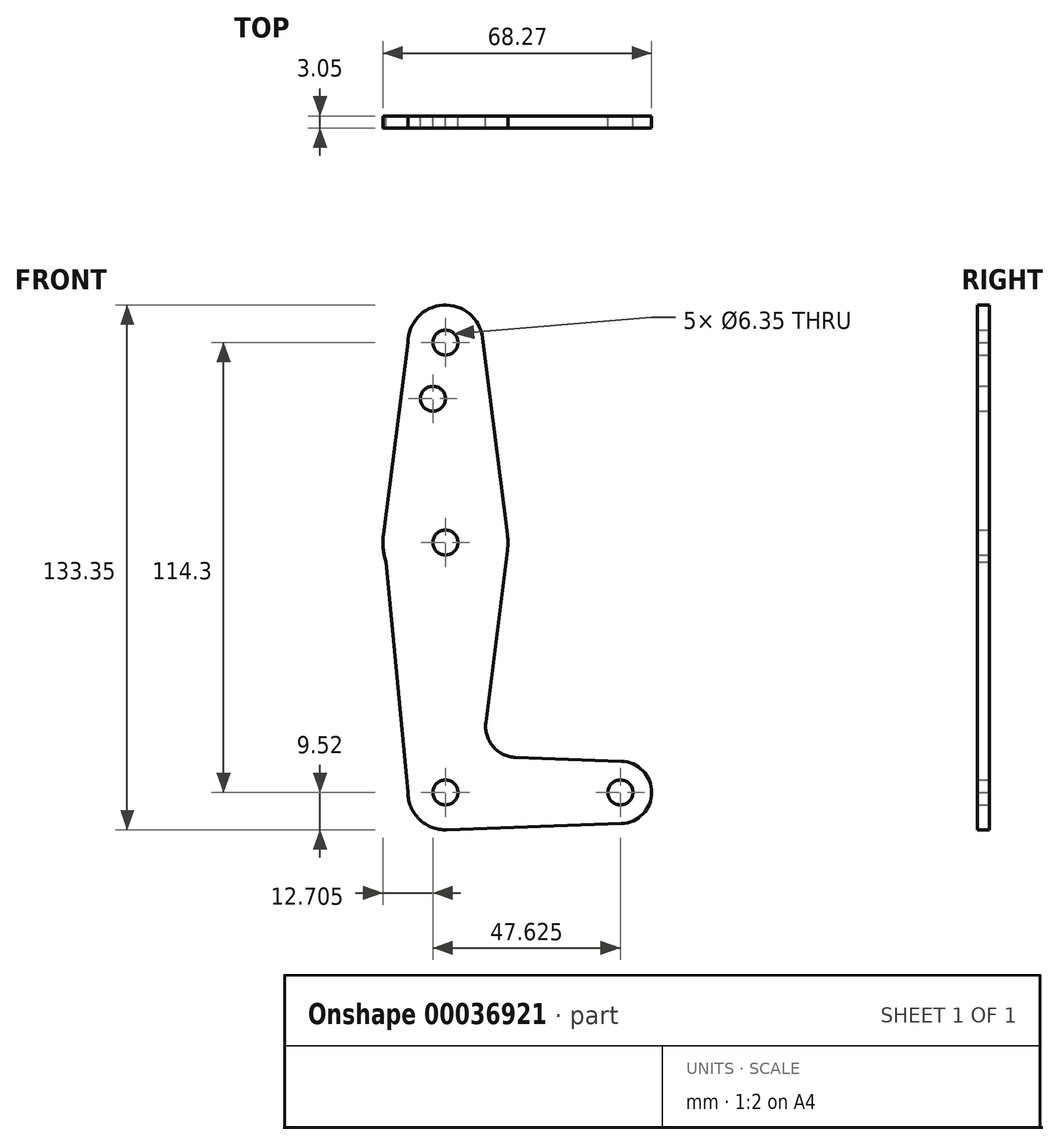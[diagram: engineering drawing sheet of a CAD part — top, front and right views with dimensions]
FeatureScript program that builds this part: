
annotation { "Feature Type Name" : "Feature", "Feature Type Description" : "" }
export const myFeature = defineFeature(function(context is Context, id is Id, definition is map)
    precondition{}
    {
        {
            var Q0;
            Q0=qCreatedBy(makeId("Front.planeOp"),FACE);
            var sketch = newSketch(context, id + "F0", { "sketchPlane" : qUnion([Q0])});
            skCircle(sketch, "E0", {"center": v(0, 63.5) * mm, "radius": 15.88 * mm});
            skCircle(sketch, "E1", {"center": v(0, 114.3) * mm, "radius": 9.53 * mm});
            skCircle(sketch, "E2", {"center": v(44.45, 0) * mm, "radius": 7.94 * mm});
            skLineSegment(sketch, "E3", {"start": v(0, 114.3) * mm, "end": v(0, 63.5) * mm});
            skLineSegment(sketch, "E4", {"start": v(0, 63.5) * mm, "end": v(0, 0) * mm});
            skLineSegment(sketch, "E5", {"start": v(0, 0) * mm, "end": v(44.45, 0) * mm});
            skLineSegment(sketch, "E6", {"start": v(-9.53, 114.3) * mm, "end": v(-15.75, 65.5) * mm});
            skLineSegment(sketch, "E7", {"start": v(-9.52, 0) * mm, "end": v(-15.75, 65.5) * mm});
            skLineSegment(sketch, "E8", {"start": v(9.45, 115.5) * mm, "end": v(15.75, 65.48) * mm});
            skLineSegment(sketch, "E9", {"start": v(15.75, 61.52) * mm, "end": v(10.25, 17.83) * mm});
            skLineSegment(sketch, "E10", {"start": v(17.85, 8.9) * mm, "end": v(44.73, 7.93) * mm});
            skLineSegment(sketch, "E11", {"start": v(0, -9.53) * mm, "end": v(44.73, -7.93) * mm});
            skCircle(sketch, "E12", {"center": v(0, 0) * mm, "radius": 9.53 * mm});
            skCircle(sketch, "E13", {"center": v(0, 114.3) * mm, "radius": 3.18 * mm});
            skCircle(sketch, "E14", {"center": v(0, 63.5) * mm, "radius": 3.18 * mm});
            skCircle(sketch, "E15", {"center": v(0, 0) * mm, "radius": 3.18 * mm});
            skCircle(sketch, "E16", {"center": v(44.45, 0) * mm, "radius": 3.18 * mm});
            skCircle(sketch, "E17", {"center": v(-3.17, 100.03) * mm, "radius": 3.18 * mm});
            skPoint(sketch, "E18.newPointA", {"position": v(8, 0) * mm});
            skArc(sketch, "E18.filletArc", {"start": v(10.25, 17.83) * mm, "mid": v(12.08, 11.69) * mm, "end": v(17.85, 8.9) * mm});
            skSolve(sketch);
        }
        {
            var Q0;
            Q0 = qSketchRegion(id + "F0", true);
            var Q1;
            {var subQ3=sQuery(id+"F0.wireOp",EDGE,"E4");var subQ5=sQuery(id+"F0.wireOp",EDGE,"E12");var subQ7=makeQuery(id+"F0.imprint","INTERSECT",VERTEX,{"derivedFrom":[subQ3,subQ5]});Q1=makeQuery(id+"F0.imprint","IMPRINT",FACE,{"disambiguationData":[TD([[makeQuery(id+"F0.imprint","IMPRINT",EDGE,{"disambiguationData":[TD([[subQ7,-1.0]])],"derivedFrom":subQ3}),1.0]])]});}
            extrude(context, id + "F1", {"entities" : qUnion([Q0, Q1]), "depth" : 3.05 * mm});
        }
    });
